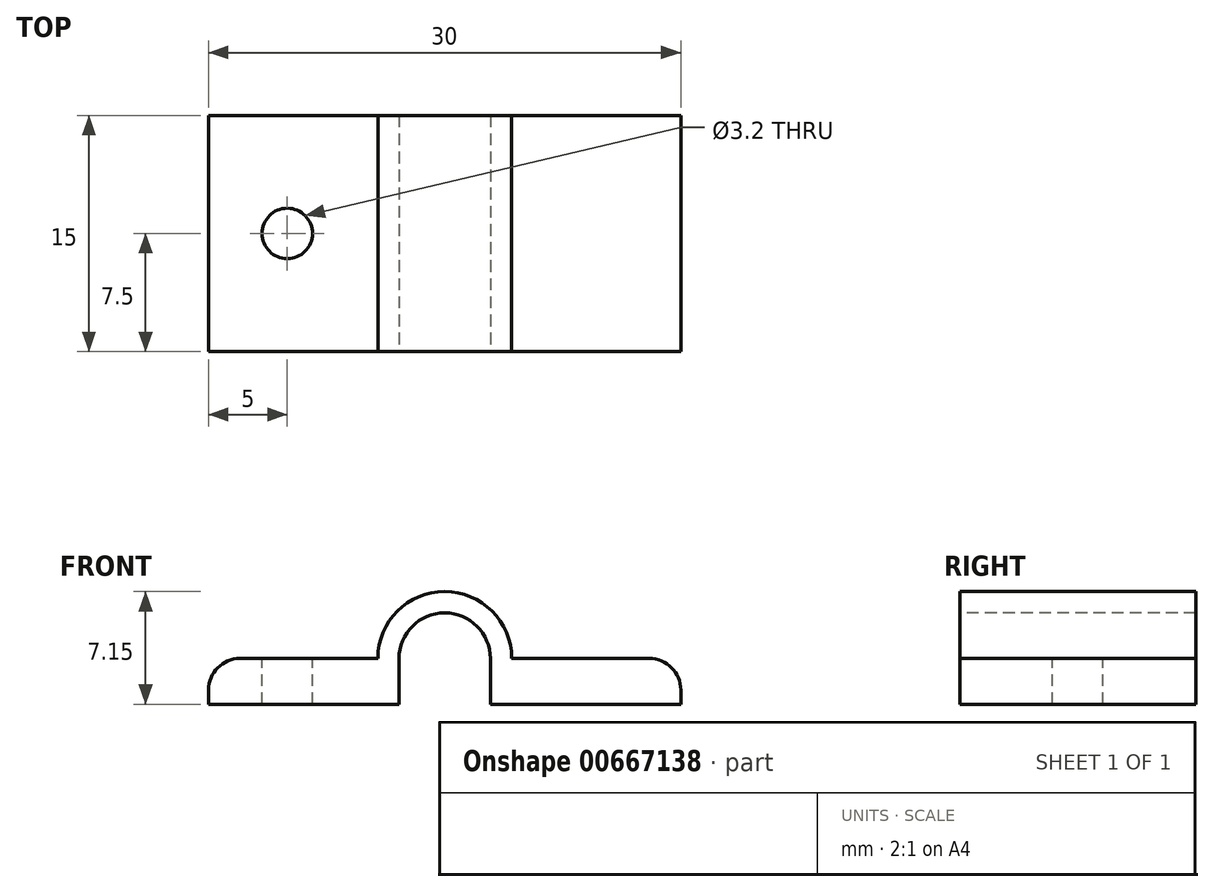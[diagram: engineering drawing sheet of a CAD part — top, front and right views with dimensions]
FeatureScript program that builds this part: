
annotation { "Feature Type Name" : "Feature", "Feature Type Description" : "" }
export const myFeature = defineFeature(function(context is Context, id is Id, definition is map)
    precondition{}
    {
        {
            var Q0;
            Q0=qCreatedBy(makeId("Front.planeOp"),FACE);
            var sketch = newSketch(context, id + "F0", { "sketchPlane" : qUnion([Q0])});
            skLineSegment(sketch, "E0.bottom", {"start": v(-15, 0) * mm, "end": v(-2.9, 0) * mm});
            skLineSegment(sketch, "E0.top", {"start": v(-15, 2.9) * mm, "end": v(-4.25, 2.9) * mm});
            skLineSegment(sketch, "E0.left", {"start": v(-15, 0) * mm, "end": v(-15, 2.9) * mm});
            skLineSegment(sketch, "E0.right", {"start": v(15, 0) * mm, "end": v(15, 2.9) * mm});
            skArc(sketch, "E1", {"start": v(2.9, 2.9) * mm, "mid": v(0, 5.8) * mm, "end": v(-2.9, 2.9) * mm});
            skArc(sketch, "E2", {"start": v(4.25, 2.9) * mm, "mid": v(0, 7.15) * mm, "end": v(-4.25, 2.9) * mm});
            skLineSegment(sketch, "E3", {"start": v(-2.9, 2.9) * mm, "end": v(-2.9, 0) * mm});
            skLineSegment(sketch, "E4", {"start": v(2.9, 2.9) * mm, "end": v(2.9, 0) * mm});
            skLineSegment(sketch, "E5.trimOffspring", {"start": v(4.25, 2.9) * mm, "end": v(15, 2.9) * mm});
            skLineSegment(sketch, "E6.trimOffspring", {"start": v(2.9, 0) * mm, "end": v(15, 0) * mm});
            skSolve(sketch);
        }
        {
            var Q0;
            Q0=makeQuery(id+"F0.imprint","IMPRINT",FACE,{"disambiguationData":[TD([[makeQuery(id+"F0.imprint","IMPRINT",EDGE,{"derivedFrom":sQuery(id+"F0.wireOp",EDGE,"E0.bottom")}),1.0]])]});
            extrude(context, id + "F1", {"entities" : qUnion([Q0]), "oppositeDirection" : true, "depth" : 15 * mm, "offsetDistance" : 25 * mm});
        }
        {
            var Q0;
            Q0=makeQuery(id+"F1.opExtrude","SWEPT_FACE",FACE,{"disambiguationData":[OSD([sQuery(id+"F0.wireOp",EDGE,"E0.top")])]});
            var sketch = newSketch(context, id + "F2", { "sketchPlane" : qUnion([Q0])});
            skPoint(sketch, "E7.centerSnap0", {"position": v(-15, 7.5) * mm});
            skCircle(sketch, "E8", {"center": v(-10, 7.5) * mm, "radius": 1.6 * mm});
            skCircle(sketch, "E9.MirrorC", {"center": v(10, 7.5) * mm, "radius": 1.6 * mm});
            skSolve(sketch);
        }
        {
            var Q0;
            Q0=makeQuery(id+"F2.imprint","IMPRINT",FACE,{"disambiguationData":[TD([[makeQuery(id+"F2.imprint","IMPRINT",EDGE,{"derivedFrom":sQuery(id+"F2.wireOp",EDGE,"E8")}),1.0]])]});
            var Q1;
            Q1=makeQuery(id+"F2.imprint","IMPRINT",FACE,{"disambiguationData":[TD([[makeQuery(id+"F2.imprint","IMPRINT",EDGE,{"derivedFrom":sQuery(id+"F2.wireOp",EDGE,"E9.MirrorC")}),-1.0]])]});
            extrude(context, id + "F3", {"entities" : qUnion([Q0, Q1]), "operationType" : NewBodyOperationType.REMOVE, "endBound" : BoundingType.THROUGH_ALL, "oppositeDirection" : true, "depth" : 25 * mm, "offsetDistance" : 25 * mm});
        }
        {
            var Q0;
            Q0=makeQuery(id+"F1.opExtrude","SWEPT_EDGE",EDGE,{"disambiguationData":[OSD([sQuery(id+"F0.wireOp",EDGE,"E0.top"),sQuery(id+"F0.wireOp",EDGE,"E0.left")])]});
            var Q1;
            Q1=makeQuery(id+"F1.opExtrude","SWEPT_EDGE",EDGE,{"disambiguationData":[OSD([sQuery(id+"F0.wireOp",EDGE,"E0.right"),sQuery(id+"F0.wireOp",EDGE,"E5.trimOffspring")])]});
            fillet(context, id + "F4", {"entities" : qUnion([Q0, Q1]), "radius" : 2 * mm, "tangentPropagation" : true, "allowEdgeOverflow" : false});
        }
    });
